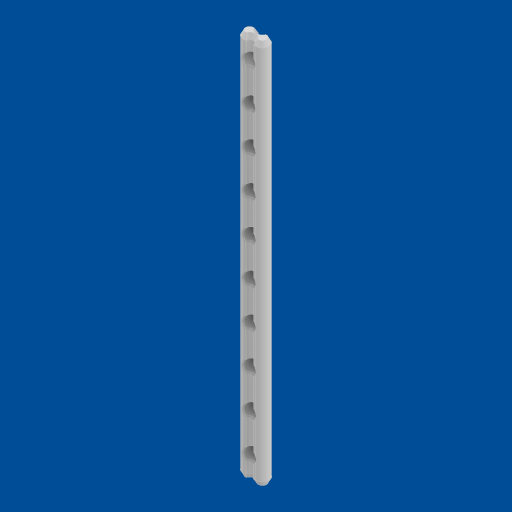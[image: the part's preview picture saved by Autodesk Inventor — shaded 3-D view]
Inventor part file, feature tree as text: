
AUTODESK INVENTOR PART (.ipt)
format: ipt  version: 2023 (Build 270158000, 158)  size: 247,296 bytes
history: native  units: mm
features: chamfer x8, extrude x2, sketch x2
ambient origin geometry x8: Origin, YZ Plane, XZ Plane, XY Plane, X Axis, Y Axis, Z Axis, Center Point
bodies: Solid1 (feature_tree)
feature tree (12):
  extrude  "Extrusion1"  Depth=11.0mm
  chamfer  "Chamfer1"  Distance=15.0mm
  chamfer  "Chamfer2"  Distance=6.5mm
  chamfer  "Chamfer3"  Distance=325.0mm
  chamfer  "Chamfer4"  Distance=2.0mm Angle=30.0deg
  chamfer  "Chamfer5"  Distance=2.0mm Angle=30.0deg
  chamfer  "Chamfer6"  Distance=2.0mm Angle=30.0deg
  chamfer  "Chamfer7"  Distance=2.0mm Angle=30.0deg
  chamfer  "Chamfer8"  Distance=2.0mm Angle=30.0deg
  extrude  "Extrusion2"  Depth=10.0mm TaperAngle=30.0deg
  sketch  "Sketch1"  dims[d0=11.0mm d1=11.0mm]
  sketch  "Sketch2"  dims[d2=15.0mm d3=15.0mm d4=6.5mm d5=325.0mm d6=0.0mm d7=2.0mm d8=4.0mm d9=30.0deg d10=2.0mm d11=4.0mm d12=30.0deg d13=2.0mm d14=4.0mm d15=30.0deg d16=2.0mm d17=4.0mm d18=30.0deg d19=2.0mm d20=4.0mm d21=30.0deg d22=4.0mm d23=2.0mm d24=30.0deg d25=4.0mm d26=2.0mm d27=30.0deg d28=4.0mm d29=2.0mm d30=30.0deg d31=15.0mm d32=11.0mm d33=100.0mm d35=32.0mm d36=10.0mm d38=10.0mm d40=20.0mm d41=0.0mm]
